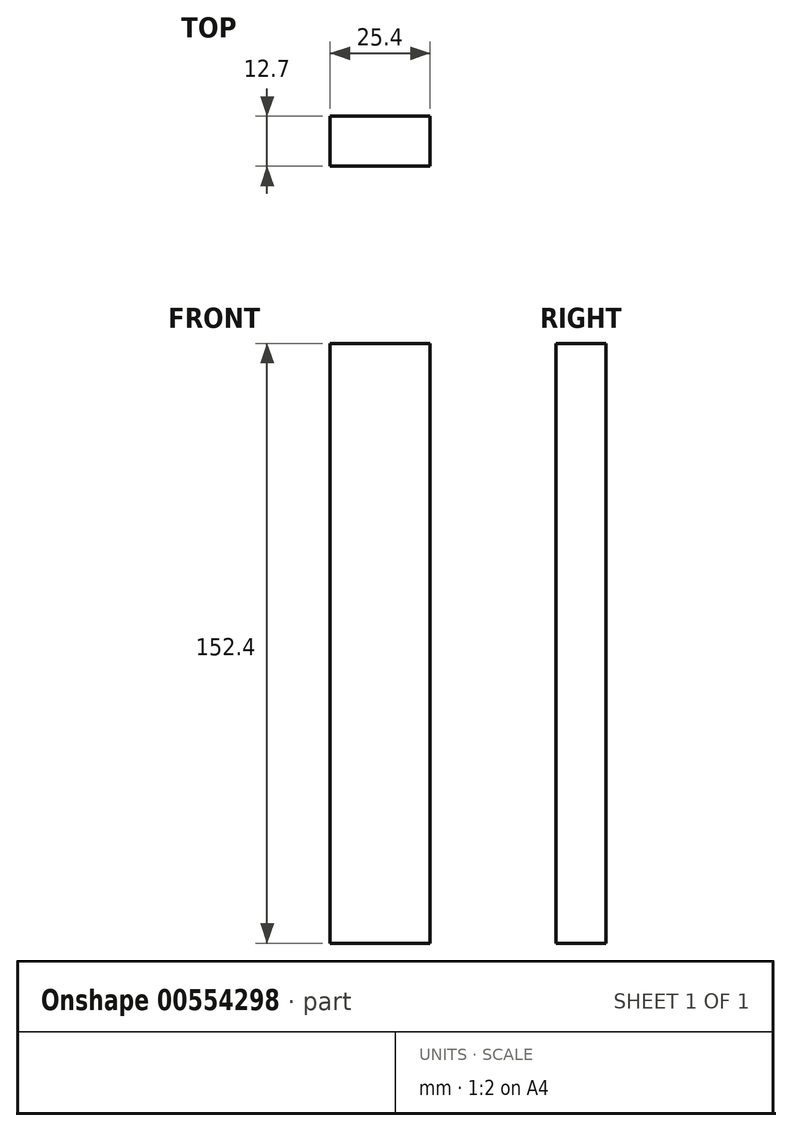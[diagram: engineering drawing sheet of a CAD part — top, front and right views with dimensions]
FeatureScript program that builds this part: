
annotation { "Feature Type Name" : "Feature", "Feature Type Description" : "" }
export const myFeature = defineFeature(function(context is Context, id is Id, definition is map)
    precondition{}
    {
        {
            var Q0;
            Q0=qCreatedBy(makeId("Front.planeOp"),FACE);
            var sketch = newSketch(context, id + "F0", { "sketchPlane" : qUnion([Q0])});
            skLineSegment(sketch, "E0.bottom", {"start": v(-5.96, 74.9) * mm, "end": v(19.44, 74.9) * mm});
            skLineSegment(sketch, "E0.top", {"start": v(-5.96, -77.5) * mm, "end": v(19.44, -77.5) * mm});
            skLineSegment(sketch, "E0.left", {"start": v(-5.96, 74.9) * mm, "end": v(-5.96, -77.5) * mm});
            skLineSegment(sketch, "E0.right", {"start": v(19.44, 74.9) * mm, "end": v(19.44, -77.5) * mm});
            skSolve(sketch);
        }
        {
            var Q0;
            Q0 = qSketchRegion(id + "F0", true);
            extrude(context, id + "F1", {"entities" : qUnion([Q0]), "depth" : 12.7 * mm, "offsetDistance" : 25.4 * mm});
        }
    });
